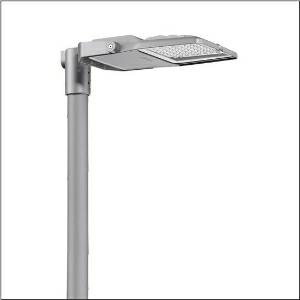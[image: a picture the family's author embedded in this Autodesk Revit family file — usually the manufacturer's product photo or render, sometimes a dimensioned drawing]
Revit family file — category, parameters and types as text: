
# Revit family: floodlight_fl_21_mini___pl52_5xa7771b2d3a_629a
name_source: partatom
category: Lighting Fixtures
units: mm (PartAtom-declared; Revit-internal decimal feet)

## family parameters
Cut with Voids When Loaded = No
Host = Face
Light Source = No
Part Type = Normal
Room Calculation Point = No
Round Connector Dimension = Use Diameter
Shared = No

## types (1)
- --- (1 x LED, 6240 lm, 45.5 W, 3000K)
    Apparent Load = 46 VA
    CIE Flux Codes = 26 60 98 100 100
    Color Rendering = 70
    Color Temperature = 3000K
    Default Elevation = 1800 mm
    Description = Floodlight FL 21 mini, floodlight, primary light control with lens, of PMMA, primary optical cover: protective disc, of toughened safety glass, transparent, light distribution: PL52, light emission: direct distribution, installation type: surface-mounted, LED, High Power LED, rated luminous flux: 6.240lm, luminous efficacy: 137lm/W, light colour: 730, colour temperature: 3000K, control gear: ECG iQ, control: Auto-Match, Temp-Guard, Lumen-Switch, Night-Set, Smart-Wire, Light-Fading, Desk-Remote (wireless, voltage-free reading and setting of iQ features in the workshop via application-optimized NFC function/RFID function), optimised constant luminous flux control (CLO 2.0), with terminal, 6-pole, mains connection: 220..240V, AC, 50/60Hz, start of lifetime: 46W, end of lifetime: 48W, reduction: 22W, luminaire housing, of diecast aluminium, powder-coated, Siteco® metallic grey (DB 702S), corrosivity category C5 according to DIN EN ISO 12944, mast bracket, of steel, galvanised, powder-coated, Siteco® metallic grey (DB 702S), protection rating (complete): IP66, insulation class (complete): insulation class II (safety insulation), certification: CE, ENEC, VDE, protection symbol: D, impact resistance: IK08, permissible operating ambient temperature: -40..+40°C, permissible operating ambient temperature for outdoor applications: -40..+50°C, standard: DIN EN 12944, packaging unit: 1 piece

Light Distribution: PL52
    Height = 70 mm
    Lamp = 1 x LED
    Lamp Light Flux = 6240 lm
    Lamp Power = 45.5 W
    Lamp count = 1
    Length = 485 mm
    Luminous efficacy = 137 lm/W
    Manufacturer = Siteco
    ModVariant = No
    Model = 5XA7771B2D3A
    Number of Poles = 1
    OnlyDefault = Yes
    Power Factor = 1
    Product Name = Floodlight FL 21 mini | PL52
    Product group = floodlight | pylon top
    ProductGroupID = 6101
    Protection Class = Protection class II
    Protection Degree = IP 66
    RLX_Detail_Level = 1
    RlxData = <blob elided: 101229 chars, md5=ab47a0d0>
    Socket = socket
    Standby Power = 0 W
    System Light Flux = 6240 lm
    System Power = 46 W
    Type Comments = factory setting: luminous flux: 100 % | dim-lin: 254 | 463 mA
    Type Image = l_1007125.jpg
    URL = http://relux.com
    VarID = @adj_076215
    Voltage = 0 V
    Weight = 0.00 kg
    Width = 337 mm

## geometry (parser evidence)
native form markers: Blend x4, Sweep x12
no freeform markers — native parametric forms only
